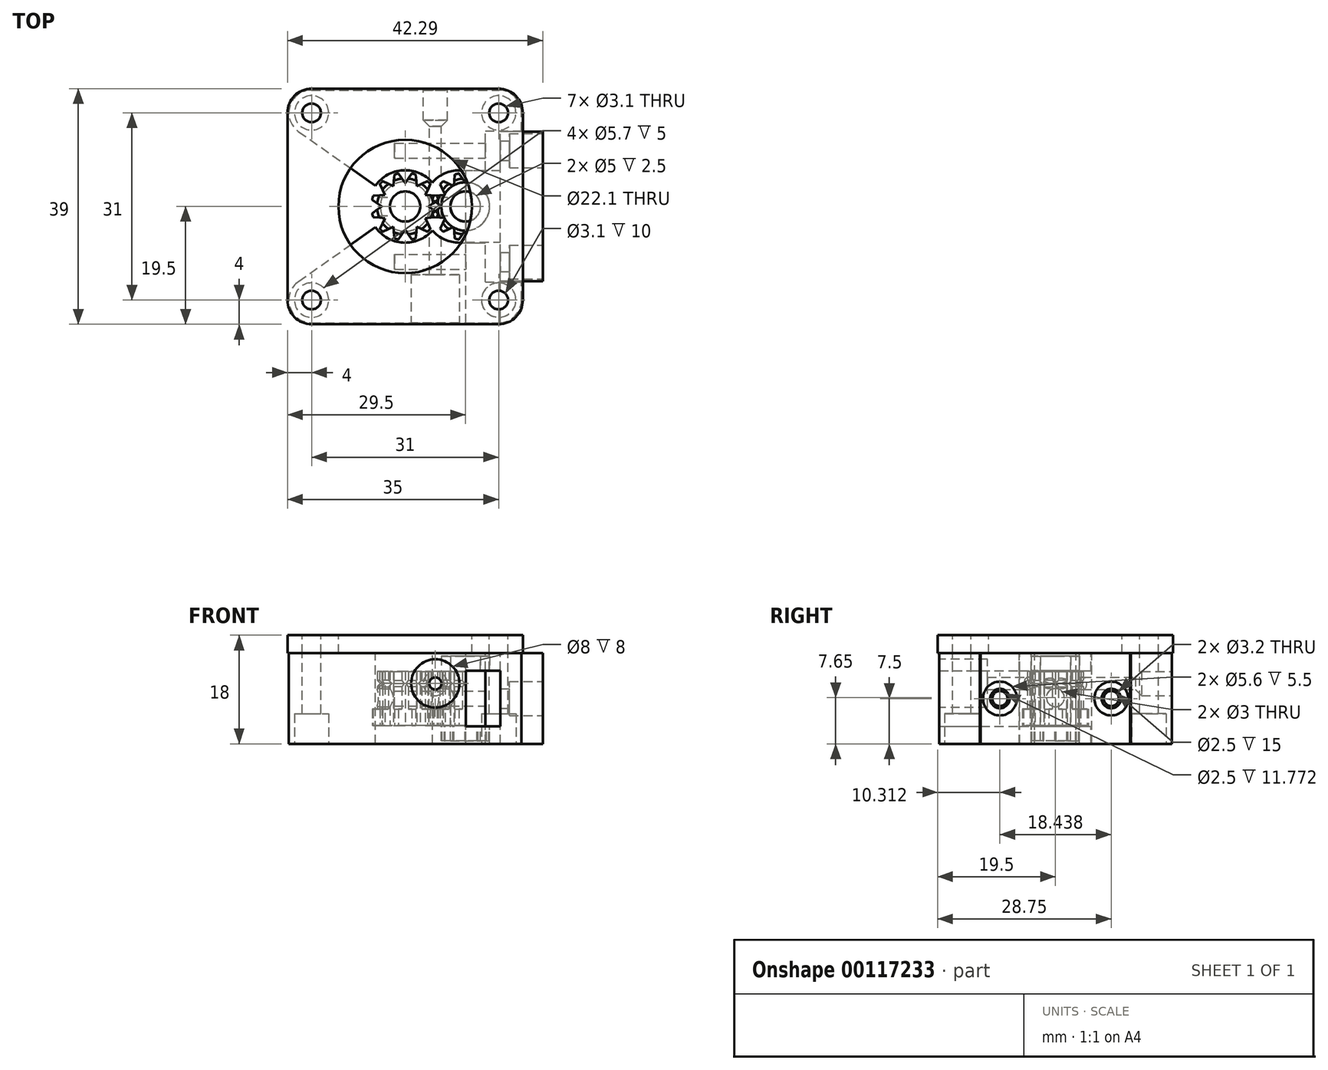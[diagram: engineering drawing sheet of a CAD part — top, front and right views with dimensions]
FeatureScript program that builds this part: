
annotation { "Feature Type Name" : "Feature", "Feature Type Description" : "" }
export const myFeature = defineFeature(function(context is Context, id is Id, definition is map)
    precondition{}
    {
        {
            var Q0;
            Q0=qCreatedBy(makeId("Top.planeOp"),FACE);
            var sketch = newSketch(context, id + "F0", { "sketchPlane" : qUnion([Q0])});
            skCircle(sketch, "E0", {"center": v(0, 0) * mm, "radius": 2.5 * mm});
            skCircle(sketch, "E1", {"center": v(0, 0) * mm, "radius": 5.58 * mm});
            skSolve(sketch);
        }
        {
            var Q0;
            Q0=makeQuery(id+"F0.imprint","IMPRINT",FACE,{"disambiguationData":[TD([[makeQuery(id+"F0.imprint","IMPRINT",EDGE,{"derivedFrom":sQuery(id+"F0.wireOp",EDGE,"E0")}),-1.0]])]});
            extrude(context, id + "F1", {"entities" : qUnion([Q0]), "depth" : 2.75 * mm});
        }
        {
            var Q0;
            Q0=makeQuery(id+"F1.opExtrude","CAP_FACE",FACE,{"disambiguationData":[OSD([sQuery(id+"F0.wireOp",EDGE,"E0"),sQuery(id+"F0.wireOp",EDGE,"E1")])],"isStart":false});
            var sketch = newSketch(context, id + "F2", { "sketchPlane" : qUnion([Q0])});
            skCircle(sketch, "E2", {"center": v(0, 0) * mm, "radius": 2.5 * mm});
            skCircle(sketch, "E3", {"center": v(0, 0) * mm, "radius": 4.65 * mm});
            skSolve(sketch);
        }
        {
            var Q0;
            Q0=makeQuery(id+"F2.imprint","IMPRINT",FACE,{"disambiguationData":[TD([[makeQuery(id+"F2.imprint","IMPRINT",EDGE,{"derivedFrom":sQuery(id+"F2.wireOp",EDGE,"E2")}),-1.0]])]});
            extrude(context, id + "F3", {"entities" : qUnion([Q0]), "operationType" : NewBodyOperationType.ADD, "depth" : (9 - 2.75) * mm});
        }
        {
            var Q0;
            Q0=qCreatedBy(makeId("Right.planeOp"),FACE);
            var sketch = newSketch(context, id + "F4", { "sketchPlane" : qUnion([Q0])});
            skLineSegment(sketch, "E4", {"start": v(0, -4.4) * mm, "end": v(0, 15.22) * mm, "construction": true});
            skLineSegment(sketch, "E5", {"start": v(4.1, 14.73) * mm, "end": v(4.1, -6.8) * mm, "construction": true});
            skLineSegment(sketch, "E6", {"start": v(6.69, 7) * mm, "end": v(-11.79, 7) * mm, "construction": true});
            skLineSegment(sketch, "E7", {"start": v(4.1, 7) * mm, "end": v(5.02, 7.92) * mm});
            skLineSegment(sketch, "E8", {"start": v(4.1, 7) * mm, "end": v(5.2, 5.9) * mm});
            skLineSegment(sketch, "E9", {"start": v(5.02, 7.92) * mm, "end": v(5.2, 5.9) * mm});
            skSolve(sketch);
        }
        {
            var Q0;
            Q0=makeQuery(id+"F4.imprint","IMPRINT",FACE,{"disambiguationData":[TD([[makeQuery(id+"F4.imprint","IMPRINT",EDGE,{"derivedFrom":sQuery(id+"F4.wireOp",EDGE,"E7")}),-1.0]])]});
            var Q1;
            Q1=sQuery(id+"F4.wireOp",EDGE,"E4");
            revolve(context, id + "F5", {"operationType" : NewBodyOperationType.REMOVE, "entities" : qUnion([Q0]), "axis" : qUnion([Q1]), "revolveType" : RevolveType.FULL, "oppositeDirection" : true});
        }
        {
            var Q0;
            Q0=qCreatedBy(makeId("Right.planeOp"),FACE);
            var sketch = newSketch(context, id + "F6", { "sketchPlane" : qUnion([Q0])});
            skCircle(sketch, "E10", {"center": v(0, 4.65) * mm, "radius": 1.5 * mm});
            skSolve(sketch);
        }
        {
            var Q0;
            Q0=makeQuery(id+"F6.imprint","IMPRINT",FACE,{"disambiguationData":[TD([[makeQuery(id+"F6.imprint","IMPRINT",EDGE,{"derivedFrom":sQuery(id+"F6.wireOp",EDGE,"E10")}),1.0]])]});
            extrude(context, id + "F7", {"entities" : qUnion([Q0]), "operationType" : NewBodyOperationType.REMOVE, "oppositeDirection" : true, "depth" : 25 * mm});
        }
        {
            var Q0;
            Q0=makeQuery(id+"F1.opExtrude","CAP_FACE",FACE,{"disambiguationData":[OSD([sQuery(id+"F0.wireOp",EDGE,"E0"),sQuery(id+"F0.wireOp",EDGE,"E1")])],"isStart":true});
            var sketch = newSketch(context, id + "F8", { "sketchPlane" : qUnion([Q0])});
            skCircle(sketch, "E11", {"center": v(0, 0) * mm, "radius": 3.88 * mm});
            skLineSegment(sketch, "E12", {"start": v(-1.69, 6.28) * mm, "end": v(0, 3.88) * mm});
            skLineSegment(sketch, "E13", {"start": v(0, 3.88) * mm, "end": v(1.69, 6.28) * mm});
            skArc(sketch, "E14", {"start": v(1.69, 6.28) * mm, "mid": v(0, 6.5) * mm, "end": v(-1.69, 6.28) * mm});
            skLineSegment(sketch, "E15.1.0", {"start": v(-1.94, 3.36) * mm, "end": v(-1.68, 6.28) * mm});
            skLineSegment(sketch, "E15.1.1", {"start": v(-4.6, 4.6) * mm, "end": v(-1.94, 3.36) * mm});
            skArc(sketch, "E15.1.2", {"start": v(-1.68, 6.28) * mm, "mid": v(-3.25, 5.63) * mm, "end": v(-4.6, 4.6) * mm});
            skLineSegment(sketch, "E15.2.0", {"start": v(-3.36, 1.94) * mm, "end": v(-4.6, 4.6) * mm});
            skLineSegment(sketch, "E15.2.1", {"start": v(-6.28, 1.68) * mm, "end": v(-3.36, 1.94) * mm});
            skArc(sketch, "E15.2.2", {"start": v(-4.6, 4.6) * mm, "mid": v(-5.63, 3.25) * mm, "end": v(-6.28, 1.68) * mm});
            skLineSegment(sketch, "E15.3.0", {"start": v(-3.88, 0) * mm, "end": v(-6.28, 1.69) * mm});
            skLineSegment(sketch, "E15.3.1", {"start": v(-6.28, -1.69) * mm, "end": v(-3.87, 0) * mm});
            skArc(sketch, "E15.3.2", {"start": v(-6.28, 1.69) * mm, "mid": v(-6.5, 0) * mm, "end": v(-6.28, -1.69) * mm});
            skLineSegment(sketch, "E15.4.0", {"start": v(-3.36, -1.94) * mm, "end": v(-6.28, -1.68) * mm});
            skLineSegment(sketch, "E15.4.1", {"start": v(-4.6, -4.6) * mm, "end": v(-3.36, -1.94) * mm});
            skArc(sketch, "E15.4.2", {"start": v(-6.28, -1.68) * mm, "mid": v(-5.63, -3.25) * mm, "end": v(-4.6, -4.6) * mm});
            skLineSegment(sketch, "E15.5.0", {"start": v(-1.94, -3.36) * mm, "end": v(-4.6, -4.6) * mm});
            skLineSegment(sketch, "E15.5.1", {"start": v(-1.68, -6.28) * mm, "end": v(-1.94, -3.36) * mm});
            skArc(sketch, "E15.5.2", {"start": v(-4.6, -4.6) * mm, "mid": v(-3.25, -5.63) * mm, "end": v(-1.68, -6.28) * mm});
            skLineSegment(sketch, "E15.6.0", {"start": v(0, -3.88) * mm, "end": v(-1.69, -6.28) * mm});
            skLineSegment(sketch, "E15.6.1", {"start": v(1.69, -6.28) * mm, "end": v(0, -3.87) * mm});
            skArc(sketch, "E15.6.2", {"start": v(-1.69, -6.28) * mm, "mid": v(0, -6.5) * mm, "end": v(1.69, -6.28) * mm});
            skLineSegment(sketch, "E15.7.0", {"start": v(1.94, -3.36) * mm, "end": v(1.68, -6.28) * mm});
            skLineSegment(sketch, "E15.7.1", {"start": v(4.6, -4.6) * mm, "end": v(1.94, -3.36) * mm});
            skArc(sketch, "E15.7.2", {"start": v(1.68, -6.28) * mm, "mid": v(3.25, -5.63) * mm, "end": v(4.6, -4.6) * mm});
            skLineSegment(sketch, "E15.8.0", {"start": v(3.36, -1.94) * mm, "end": v(4.6, -4.6) * mm});
            skLineSegment(sketch, "E15.8.1", {"start": v(6.28, -1.68) * mm, "end": v(3.36, -1.94) * mm});
            skArc(sketch, "E15.8.2", {"start": v(4.6, -4.6) * mm, "mid": v(5.63, -3.25) * mm, "end": v(6.28, -1.68) * mm});
            skLineSegment(sketch, "E15.9.0", {"start": v(3.88, 0) * mm, "end": v(6.28, -1.69) * mm});
            skLineSegment(sketch, "E15.9.1", {"start": v(6.28, 1.69) * mm, "end": v(3.87, 0) * mm});
            skArc(sketch, "E15.9.2", {"start": v(6.28, -1.69) * mm, "mid": v(6.5, 0) * mm, "end": v(6.28, 1.69) * mm});
            skLineSegment(sketch, "E15.10.0", {"start": v(3.36, 1.94) * mm, "end": v(6.28, 1.68) * mm});
            skLineSegment(sketch, "E15.10.1", {"start": v(4.6, 4.6) * mm, "end": v(3.36, 1.94) * mm});
            skArc(sketch, "E15.10.2", {"start": v(6.28, 1.68) * mm, "mid": v(5.63, 3.25) * mm, "end": v(4.6, 4.6) * mm});
            skLineSegment(sketch, "E15.11.0", {"start": v(1.94, 3.36) * mm, "end": v(4.6, 4.6) * mm});
            skLineSegment(sketch, "E15.11.1", {"start": v(1.68, 6.28) * mm, "end": v(1.94, 3.36) * mm});
            skArc(sketch, "E15.11.2", {"start": v(4.6, 4.6) * mm, "mid": v(3.25, 5.63) * mm, "end": v(1.68, 6.28) * mm});
            skSolve(sketch);
        }
        {
            var Q0;
            Q0 = qSketchRegion(id + "F8", true);
            extrude(context, id + "F9", {"entities" : qUnion([Q0]), "operationType" : NewBodyOperationType.REMOVE, "oppositeDirection" : true, "depth" : 25 * mm});
        }
        {
            var Q0;
            Q0=makeQuery(id+"F3.opExtrude","CAP_FACE",FACE,{"disambiguationData":[OSD([sQuery(id+"F2.wireOp",EDGE,"E2"),sQuery(id+"F2.wireOp",EDGE,"E3")])],"isStart":false});
            cPlane(context, id + "F10", {"entities" : qUnion([Q0]), "cplaneType" : CPlaneType.OFFSET, "offset" : 6 * mm, "width" : 150 * mm, "height" : 150 * mm});
        }
        {
            var Q0;
            Q0=qCreatedBy(id+"F10.planeOp",FACE);
            var sketch = newSketch(context, id + "F11", { "sketchPlane" : qUnion([Q0])});
            skCircle(sketch, "E16", {"center": v(0, 0) * mm, "radius": 11.05 * mm});
            skLineSegment(sketch, "E17.bottom", {"start": v(19.5, -19.5) * mm, "end": v(-19.5, -19.5) * mm});
            skLineSegment(sketch, "E17.top", {"start": v(19.5, 19.5) * mm, "end": v(-19.5, 19.5) * mm});
            skLineSegment(sketch, "E17.left", {"start": v(19.5, -19.5) * mm, "end": v(19.5, 19.5) * mm});
            skLineSegment(sketch, "E17.right", {"start": v(-19.5, -19.5) * mm, "end": v(-19.5, 19.5) * mm});
            skLineSegment(sketch, "E18.bottom", {"start": v(15.5, -15.5) * mm, "end": v(-15.5, -15.5) * mm, "construction": true});
            skLineSegment(sketch, "E18.top", {"start": v(15.5, 15.5) * mm, "end": v(-15.5, 15.5) * mm, "construction": true});
            skLineSegment(sketch, "E18.left", {"start": v(15.5, -15.5) * mm, "end": v(15.5, 15.5) * mm, "construction": true});
            skLineSegment(sketch, "E18.right", {"start": v(-15.5, -15.5) * mm, "end": v(-15.5, 15.5) * mm, "construction": true});
            skCircle(sketch, "E19", {"center": v(-15.5, 15.5) * mm, "radius": 1.55 * mm});
            skCircle(sketch, "E20.0.1.0", {"center": v(-15.5, -15.5) * mm, "radius": 1.55 * mm});
            skCircle(sketch, "E20.1.0.0", {"center": v(15.5, 15.5) * mm, "radius": 1.55 * mm});
            skCircle(sketch, "E20.1.1.0", {"center": v(15.5, -15.5) * mm, "radius": 1.55 * mm});
            skCircle(sketch, "E20.2.0.0", {"center": v(46.5, 15.5) * mm, "radius": 1.55 * mm});
            skCircle(sketch, "E20.2.1.0", {"center": v(46.5, -15.5) * mm, "radius": 1.55 * mm});
            skLineSegment(sketch, "E20.direction1", {"start": v(-15.5, 15.5) * mm, "end": v(15.5, 15.5) * mm, "construction": true});
            skLineSegment(sketch, "E20.direction2", {"start": v(-15.5, 15.5) * mm, "end": v(-15.5, -15.5) * mm, "construction": true});
            skSolve(sketch);
        }
        {
            var Q0;
            Q0=makeQuery(id+"F11.imprint","IMPRINT",FACE,{"disambiguationData":[TD([[makeQuery(id+"F11.imprint","IMPRINT",EDGE,{"derivedFrom":sQuery(id+"F11.wireOp",EDGE,"E16")}),-1.0]])]});
            extrude(context, id + "F12", {"entities" : qUnion([Q0]), "oppositeDirection" : true, "depth" : 3 * mm});
        }
        {
            var Q0;
            Q0=makeQuery(id+"F1.opExtrude","SWEPT_BODY",BODY,{"disambiguationData":[OSD([sQuery(id+"F0.wireOp",EDGE,"E0"),sQuery(id+"F0.wireOp",EDGE,"E1")])]});
            transform(context, id + "F13", {"entities" : qUnion([Q0]), "transformType" : TransformType.TRANSLATION_3D, "dx" : 10 * mm, "dy" : 0 * mm, "dz" : 0 * mm, "makeCopy" : true});
        }
        {
            var Q0;
            Q0=makeQuery(id+"F13.opPattern","COPY",FACE,{"derivedFrom":makeQuery(id+"F1.opExtrude","CAP_FACE",FACE,{"disambiguationData":[OSD([sQuery(id+"F0.wireOp",EDGE,"E0"),sQuery(id+"F0.wireOp",EDGE,"E1")])],"isStart":true}),"instanceName":"1"});
            var sketch = newSketch(context, id + "F14", { "sketchPlane" : qUnion([Q0])});
            skCircle(sketch, "E21", {"center": v(10, 0) * mm, "radius": 2.5 * mm});
            skCircle(sketch, "E22", {"center": v(10, 0) * mm, "radius": 4 * mm});
            skSolve(sketch);
        }
        {
            var Q0;
            Q0=makeQuery(id+"F14.imprint","IMPRINT",FACE,{"disambiguationData":[TD([[makeQuery(id+"F14.imprint","IMPRINT",EDGE,{"derivedFrom":sQuery(id+"F14.wireOp",EDGE,"E21")}),1.0]])]});
            extrude(context, id + "F15", {"entities" : qUnion([Q0]), "depth" : 2.5 * mm});
        }
        {
            var Q0;
            Q0=makeQuery(id+"F13.opPattern","COPY",FACE,{"derivedFrom":makeQuery(id+"F3.opExtrude","CAP_FACE",FACE,{"disambiguationData":[OSD([sQuery(id+"F2.wireOp",EDGE,"E2"),sQuery(id+"F2.wireOp",EDGE,"E3")])],"isStart":false}),"instanceName":"1"});
            var sketch = newSketch(context, id + "F16", { "sketchPlane" : qUnion([Q0])});
            skCircle(sketch, "E23", {"center": v(10, 0) * mm, "radius": 2.5 * mm});
            skCircle(sketch, "E24", {"center": v(10, 0) * mm, "radius": 4 * mm});
            skSolve(sketch);
        }
        {
            var Q0;
            Q0 = qSketchRegion(id + "F16", true);
            extrude(context, id + "F17", {"entities" : qUnion([Q0]), "depth" : 2.5 * mm});
        }
        {
            var Q0;
            Q0=makeQuery(id+"F17.opExtrude","CAP_FACE",FACE,{"disambiguationData":[OSD([sQuery(id+"F16.wireOp",EDGE,"E23"),sQuery(id+"F16.wireOp",EDGE,"E24")])],"isStart":false});
            var sketch = newSketch(context, id + "F18", { "sketchPlane" : qUnion([Q0])});
            skCircle(sketch, "E25", {"center": v(10, 0) * mm, "radius": 2.5 * mm});
            skSolve(sketch);
        }
        {
            var Q0;
            Q0 = qSketchRegion(id + "F18", true);
            var Q1;
            Q1=makeQuery(id+"F15.opExtrude","CAP_FACE",FACE,{"disambiguationData":[OSD([sQuery(id+"F8.wireOp",EDGE,"E12"),sQuery(id+"F8.wireOp",EDGE,"E13"),sQuery(id+"F8.wireOp",EDGE,"E15.1.0"),sQuery(id+"F8.wireOp",EDGE,"E15.1.1"),sQuery(id+"F8.wireOp",EDGE,"E15.2.0"),sQuery(id+"F8.wireOp",EDGE,"E15.2.1"),sQuery(id+"F8.wireOp",EDGE,"E15.3.0"),sQuery(id+"F8.wireOp",EDGE,"E15.3.1"),sQuery(id+"F8.wireOp",EDGE,"E15.4.0"),sQuery(id+"F8.wireOp",EDGE,"E15.4.1"),sQuery(id+"F8.wireOp",EDGE,"E15.5.0"),sQuery(id+"F8.wireOp",EDGE,"E15.5.1"),sQuery(id+"F8.wireOp",EDGE,"E15.6.0"),sQuery(id+"F8.wireOp",EDGE,"E15.6.1"),sQuery(id+"F8.wireOp",EDGE,"E15.7.0"),sQuery(id+"F8.wireOp",EDGE,"E15.7.1"),sQuery(id+"F8.wireOp",EDGE,"E15.8.0"),sQuery(id+"F8.wireOp",EDGE,"E15.8.1"),sQuery(id+"F8.wireOp",EDGE,"E15.9.0"),sQuery(id+"F8.wireOp",EDGE,"E15.9.1"),sQuery(id+"F8.wireOp",EDGE,"E15.10.0"),sQuery(id+"F8.wireOp",EDGE,"E15.10.1"),sQuery(id+"F8.wireOp",EDGE,"E15.11.0"),sQuery(id+"F8.wireOp",EDGE,"E15.11.1"),sQuery(id+"F14.wireOp",EDGE,"E21"),sQuery(id+"F14.wireOp",EDGE,"E22")])],"isStart":false});
            extrude(context, id + "F19", {"entities" : qUnion([Q0]), "endBound" : BoundingType.UP_TO_SURFACE, "oppositeDirection" : true, "endBoundEntityFace" : qUnion([Q1]), "depth" : 25 * mm});
        }
        {
            var Q0;
            Q0=makeQuery(id+"F12.opExtrude","CAP_FACE",FACE,{"disambiguationData":[OSD([sQuery(id+"F11.wireOp",EDGE,"E16"),sQuery(id+"F11.wireOp",EDGE,"E17.bottom"),sQuery(id+"F11.wireOp",EDGE,"E17.top"),sQuery(id+"F11.wireOp",EDGE,"E17.left"),sQuery(id+"F11.wireOp",EDGE,"E17.right"),sQuery(id+"F11.wireOp",EDGE,"E19"),sQuery(id+"F11.wireOp",EDGE,"E20.0.1.0"),sQuery(id+"F11.wireOp",EDGE,"E20.1.0.0"),sQuery(id+"F11.wireOp",EDGE,"E20.1.1.0")])],"isStart":false});
            var sketch = newSketch(context, id + "F20", { "sketchPlane" : qUnion([Q0])});
            skArc(sketch, "E26", {"start": v(4.5, 3.97) * mm, "mid": v(-0.33, 6) * mm, "end": v(-4.9, 3.45) * mm});
            skArc(sketch, "E27", {"start": v(9, 6) * mm, "mid": v(6.53, 5.47) * mm, "end": v(4.5, 3.97) * mm});
            skLineSegment(sketch, "E28.bottom", {"start": v(9, 6) * mm, "end": v(13.27, 6) * mm});
            skLineSegment(sketch, "E28.top", {"start": v(9, -6) * mm, "end": v(13.27, -6) * mm});
            skArc(sketch, "E29.trimOffspring", {"start": v(4.5, -3.97) * mm, "mid": v(6.53, -5.47) * mm, "end": v(9, -6) * mm});
            skLineSegment(sketch, "E30.bottom", {"start": v(-15.5, 19.27) * mm, "end": v(15.5, 19.27) * mm});
            skLineSegment(sketch, "E30.top", {"start": v(-15.5, -19.27) * mm, "end": v(15.5, -19.27) * mm});
            skLineSegment(sketch, "E30.right", {"start": v(19.27, 15.5) * mm, "end": v(19.27, 12.5) * mm});
            skCircle(sketch, "E31", {"center": v(15.5, 15.5) * mm, "radius": 1.55 * mm});
            skCircle(sketch, "E32", {"center": v(15.5, -15.5) * mm, "radius": 1.55 * mm});
            skCircle(sketch, "E33", {"center": v(-15.5, -15.5) * mm, "radius": 1.55 * mm});
            skArc(sketch, "E34", {"start": v(19.27, 15.5) * mm, "mid": v(18.16, 18.16) * mm, "end": v(15.5, 19.27) * mm});
            skArc(sketch, "E35", {"start": v(15.5, -19.27) * mm, "mid": v(18.16, -18.16) * mm, "end": v(19.27, -15.5) * mm});
            skArc(sketch, "E36", {"start": v(-17.67, -12.42) * mm, "mid": v(-19.1, -16.64) * mm, "end": v(-15.5, -19.27) * mm});
            skLineSegment(sketch, "E37", {"start": v(-17.67, -12.42) * mm, "end": v(-4.9, -3.45) * mm});
            skArc(sketch, "E38", {"start": v(-15.5, 19.27) * mm, "mid": v(-19.1, 16.64) * mm, "end": v(-17.67, 12.42) * mm});
            skLineSegment(sketch, "E39", {"start": v(-17.67, 12.42) * mm, "end": v(-4.9, 3.45) * mm});
            skArc(sketch, "E40.trimOffspring", {"start": v(-4.9, -3.45) * mm, "mid": v(-0.33, -6) * mm, "end": v(4.5, -3.97) * mm});
            skLineSegment(sketch, "E41.bottom", {"start": v(13.27, 12.5) * mm, "end": v(19.27, 12.5) * mm});
            skLineSegment(sketch, "E41.top", {"start": v(13.27, -12.5) * mm, "end": v(19.27, -12.5) * mm});
            skLineSegment(sketch, "E41.left", {"start": v(13.27, 12.5) * mm, "end": v(13.27, 6) * mm});
            skPoint(sketch, "E41.middle", {"position": v(19.27, 0) * mm});
            skPoint(sketch, "E41.cornerSnap0", {"position": v(13.27, 6) * mm});
            skLineSegment(sketch, "E42.trimOffspring", {"start": v(13.27, -6) * mm, "end": v(13.27, -12.5) * mm});
            skPoint(sketch, "E28.right.start.orphan", {"position": v(17.53, 6) * mm});
            skPoint(sketch, "E41.right.end.orphan", {"position": v(25.27, -12.5) * mm});
            skPoint(sketch, "E41.right.start.orphan", {"position": v(25.27, 12.5) * mm});
            skLineSegment(sketch, "E43.trimOffspring", {"start": v(19.27, -12.5) * mm, "end": v(19.27, -15.5) * mm});
            skSolve(sketch);
        }
        {
            var Q0;
            Q0=makeQuery(id+"F20.imprint","IMPRINT",FACE,{"disambiguationData":[TD([[makeQuery(id+"F20.imprint","IMPRINT",EDGE,{"derivedFrom":sQuery(id+"F20.wireOp",EDGE,"E30.bottom")}),-1.0]])]});
            var Q1;
            {var subQ4=sQuery(id+"F20.wireOp",EDGE,"E29.trimOffspring");Q1=makeQuery(id+"F20.imprint","IMPRINT",FACE,{"disambiguationData":[TD([[makeQuery(id+"F20.imprint","IMPRINT",EDGE,{"derivedFrom":subQ4}),-1.0]])]});}
            var Q2;
            Q2=makeQuery(id+"F20.imprint","IMPRINT",FACE,{"disambiguationData":[TD([[makeQuery(id+"F20.imprint","IMPRINT",EDGE,{"derivedFrom":sQuery(id+"F20.wireOp",EDGE,"E30.top")}),1.0]])]});
            var Q3;
            {var subQ5=sQuery(id+"F20.wireOp",EDGE,"E26");Q3=makeQuery(id+"F20.imprint","IMPRINT",FACE,{"disambiguationData":[TD([[makeQuery(id+"F20.imprint","IMPRINT",EDGE,{"derivedFrom":subQ5}),-1.0]])]});}
            extrude(context, id + "F21", {"entities" : qUnion([Q0, Q1, Q2, Q3]), "depth" : 15 * mm});
        }
        {
            var Q0;
            Q0=makeQuery(id+"F20.imprint","IMPRINT",FACE,{"disambiguationData":[TD([[makeQuery(id+"F20.imprint","IMPRINT",EDGE,{"derivedFrom":sQuery(id+"F20.wireOp",EDGE,"E30.top")}),1.0]])]});
            extrude(context, id + "F22", {"entities" : qUnion([Q0]), "depth" : 15 * mm});
        }
        {
            var Q0;
            Q0=makeQuery(id+"F22.opExtrude","SWEPT_FACE",FACE,{"disambiguationData":[OSD([sQuery(id+"F20.wireOp",EDGE,"E42.trimOffspring")])]});
            var sketch = newSketch(context, id + "F23", { "sketchPlane" : qUnion([Q0])});
            skLineSegment(sketch, "E44", {"start": v(12.5, 12) * mm, "end": v(6, -3) * mm, "construction": true});
            skLineSegment(sketch, "E45", {"start": v(-12.35, 12) * mm, "end": v(-6.02, -3) * mm, "construction": true});
            skCircle(sketch, "E46", {"center": v(9.25, 4.5) * mm, "radius": 1.25 * mm});
            skCircle(sketch, "E47", {"center": v(-9.19, 4.5) * mm, "radius": 1.25 * mm});
            skSolve(sketch);
        }
        {
            var Q0;
            Q0 = qSketchRegion(id + "F23", true);
            extrude(context, id + "F24", {"entities" : qUnion([Q0]), "operationType" : NewBodyOperationType.REMOVE, "oppositeDirection" : true, "depth" : 15 * mm});
        }
        {
            var Q0;
            Q0=makeQuery(id+"F20.imprint","IMPRINT",FACE,{"disambiguationData":[TD([[makeQuery(id+"F20.imprint","IMPRINT",EDGE,{"derivedFrom":sQuery(id+"F20.wireOp",EDGE,"E30.bottom")}),1.0]])]});
            var sketch = newSketch(context, id + "F25", { "sketchPlane" : qUnion([Q0])});
            skLineSegment(sketch, "E48.bottom", {"start": v(10.04, 5.9) * mm, "end": v(15.79, 5.9) * mm});
            skLineSegment(sketch, "E48.top", {"start": v(10.04, -5.9) * mm, "end": v(15.79, -5.9) * mm});
            skLineSegment(sketch, "E48.left", {"start": v(10.04, 5.9) * mm, "end": v(10.04, 4) * mm});
            skPoint(sketch, "E48.middle", {"position": v(19.29, 0) * mm});
            skLineSegment(sketch, "E49.trimOffspring", {"start": v(10.04, -4) * mm, "end": v(10.04, -5.9) * mm});
            skLineSegment(sketch, "E50.bottom", {"start": v(22.79, 12.38) * mm, "end": v(15.79, 12.38) * mm});
            skLineSegment(sketch, "E50.top", {"start": v(22.79, -12.38) * mm, "end": v(15.79, -12.38) * mm});
            skLineSegment(sketch, "E50.left", {"start": v(22.79, 12.38) * mm, "end": v(22.79, -12.38) * mm});
            skLineSegment(sketch, "E50.right", {"start": v(15.79, 12.38) * mm, "end": v(15.79, 5.9) * mm});
            skLineSegment(sketch, "E51.trimOffspring", {"start": v(15.79, -5.9) * mm, "end": v(15.79, -12.38) * mm});
            skPoint(sketch, "E48.right.start.orphan", {"position": v(28.54, 5.9) * mm});
            skPoint(sketch, "E52.trimOffspring.end.orphan", {"position": v(28.54, -5.9) * mm});
            skArc(sketch, "E53", {"start": v(10.04, -4) * mm, "mid": v(14, 0) * mm, "end": v(10.04, 4) * mm});
            skSolve(sketch);
        }
        {
            var Q0;
            Q0 = qSketchRegion(id + "F25", true);
            extrude(context, id + "F26", {"entities" : qUnion([Q0]), "depth" : 15 * mm});
        }
        {
            var Q0;
            Q0=makeQuery(id+"F26.opExtrude","SWEPT_FACE",FACE,{"disambiguationData":[OSD([sQuery(id+"F25.wireOp",EDGE,"E50.left")])]});
            var sketch = newSketch(context, id + "F27", { "sketchPlane" : qUnion([Q0])});
            skCircle(sketch, "E54", {"center": v(-9.19, 4.5) * mm, "radius": 1.6 * mm});
            skCircle(sketch, "E55", {"center": v(9.25, 4.5) * mm, "radius": 1.6 * mm});
            skSolve(sketch);
        }
        {
            var Q0;
            Q0 = qSketchRegion(id + "F27", true);
            extrude(context, id + "F28", {"entities" : qUnion([Q0]), "operationType" : NewBodyOperationType.REMOVE, "oppositeDirection" : true, "depth" : 8 * mm});
        }
        {
            var Q0;
            Q0=makeQuery(id+"F26.opExtrude","SWEPT_FACE",FACE,{"disambiguationData":[OSD([sQuery(id+"F25.wireOp",EDGE,"E50.left")])]});
            var sketch = newSketch(context, id + "F29", { "sketchPlane" : qUnion([Q0])});
            skCircle(sketch, "E56", {"center": v(-9.19, 4.5) * mm, "radius": 2.8 * mm});
            skCircle(sketch, "E57", {"center": v(9.25, 4.5) * mm, "radius": 2.8 * mm});
            skSolve(sketch);
        }
        {
            var Q0;
            Q0 = qSketchRegion(id + "F29", true);
            extrude(context, id + "F30", {"entities" : qUnion([Q0]), "operationType" : NewBodyOperationType.REMOVE, "oppositeDirection" : true, "depth" : 5.5 * mm});
        }
        {
            var Q0;
            Q0=makeQuery(id+"F22.opExtrude","SWEPT_BODY",BODY,{"disambiguationData":[OSD([sQuery(id+"F11.wireOp",EDGE,"E16"),sQuery(id+"F20.wireOp",EDGE,"E28.top"),sQuery(id+"F20.wireOp",EDGE,"E30.top"),sQuery(id+"F20.wireOp",EDGE,"E32"),sQuery(id+"F20.wireOp",EDGE,"E33"),sQuery(id+"F20.wireOp",EDGE,"E35"),sQuery(id+"F20.wireOp",EDGE,"E36"),sQuery(id+"F20.wireOp",EDGE,"E37"),sQuery(id+"F20.wireOp",EDGE,"E41.top"),sQuery(id+"F20.wireOp",EDGE,"E42.trimOffspring"),sQuery(id+"F20.wireOp",EDGE,"E43.trimOffspring")])]});
            deleteBodies(context, id + "F31", {"entities" : qUnion([Q0])});
        }
        {
            var Q0;
            Q0=makeQuery(id+"F21.opExtrude","SWEPT_FACE",FACE,{"disambiguationData":[OSD([sQuery(id+"F20.wireOp",EDGE,"E30.top")])]});
            var sketch = newSketch(context, id + "F32", { "sketchPlane" : qUnion([Q0])});
            skLineSegment(sketch, "E58", {"start": v(-7.91, 7) * mm, "end": v(6.12, 7) * mm, "construction": true});
            skLineSegment(sketch, "E59", {"start": v(-5, 17.58) * mm, "end": v(-5, -8.26) * mm, "construction": true});
            skCircle(sketch, "E60", {"center": v(-5, 7) * mm, "radius": 1 * mm});
            skSolve(sketch);
        }
        {
            var Q0;
            Q0 = qSketchRegion(id + "F32", true);
            extrude(context, id + "F33", {"entities" : qUnion([Q0]), "operationType" : NewBodyOperationType.REMOVE, "endBound" : BoundingType.THROUGH_ALL, "oppositeDirection" : true, "depth" : 25 * mm});
        }
        {
            var Q0;
            Q0=makeQuery(id+"F21.opExtrude","SWEPT_FACE",FACE,{"disambiguationData":[OSD([sQuery(id+"F20.wireOp",EDGE,"E30.bottom")])]});
            var sketch = newSketch(context, id + "F34", { "sketchPlane" : qUnion([Q0])});
            skLineSegment(sketch, "E61", {"start": v(-15.5, 7) * mm, "end": v(15.5, 7) * mm, "construction": true});
            skLineSegment(sketch, "E62", {"start": v(5, 21.97) * mm, "end": v(5, -13.87) * mm, "construction": true});
            skLineSegment(sketch, "E63", {"start": v(0, 22.79) * mm, "end": v(0, -28.24) * mm, "construction": true});
            skPoint(sketch, "E63.endSnap0", {"position": v(0, -3) * mm});
            skCircle(sketch, "E64", {"center": v(5, 7) * mm, "radius": 1 * mm});
            skSolve(sketch);
        }
        {
            var Q0;
            Q0 = qSketchRegion(id + "F34", true);
            extrude(context, id + "F35", {"entities" : qUnion([Q0]), "operationType" : NewBodyOperationType.REMOVE, "endBound" : BoundingType.THROUGH_ALL, "oppositeDirection" : true, "depth" : 25 * mm});
        }
        {
            var Q0;
            Q0=makeQuery(id+"F21.opExtrude","SWEPT_FACE",FACE,{"disambiguationData":[OSD([sQuery(id+"F20.wireOp",EDGE,"E30.bottom")])]});
            var sketch = newSketch(context, id + "F36", { "sketchPlane" : qUnion([Q0])});
            skCircle(sketch, "E65", {"center": v(5, 7) * mm, "radius": 4 * mm});
            skSolve(sketch);
        }
        {
            var Q0;
            Q0 = qSketchRegion(id + "F36", true);
            extrude(context, id + "F37", {"entities" : qUnion([Q0]), "operationType" : NewBodyOperationType.REMOVE, "oppositeDirection" : true, "depth" : 8 * mm});
        }
        {
            var Q0;
            Q0=makeQuery(id+"F21.opExtrude","SWEPT_FACE",FACE,{"disambiguationData":[OSD([sQuery(id+"F20.wireOp",EDGE,"E30.top")])]});
            var sketch = newSketch(context, id + "F38", { "sketchPlane" : qUnion([Q0])});
            skCircle(sketch, "E66", {"center": v(-5, 7) * mm, "radius": 2 * mm});
            skSolve(sketch);
        }
        {
            var Q0;
            Q0 = qSketchRegion(id + "F38", true);
            extrude(context, id + "F39", {"entities" : qUnion([Q0]), "operationType" : NewBodyOperationType.REMOVE, "oppositeDirection" : true, "depth" : 4 * mm});
        }
        {
            var Q0;
            Q0=makeQuery(id+"F39.boolean.opBoolean","INTERSECT",EDGE,{"derivedFrom":[makeQuery(id+"F33.boolean.opBoolean","COPY",FACE,{"derivedFrom":makeQuery(id+"F33.opExtrude","SWEPT_FACE",FACE,{"disambiguationData":[OSD([sQuery(id+"F32.wireOp",EDGE,"E60")])]})}),makeQuery(id+"F39.opExtrude","CAP_FACE",FACE,{"disambiguationData":[OSD([sQuery(id+"F38.wireOp",EDGE,"E66")])],"isStart":false})]});
            chamfer(context, id + "F40", {"entities" : qUnion([Q0]), "width" : 2 * mm, "tangentPropagation" : true});
        }
        {
            var Q0;
            Q0=makeQuery(id+"F21.opExtrude","CAP_FACE",FACE,{"disambiguationData":[OSD([sQuery(id+"F11.wireOp",EDGE,"E20.0.1.0"),sQuery(id+"F20.wireOp",EDGE,"E26"),sQuery(id+"F20.wireOp",EDGE,"E27"),sQuery(id+"F20.wireOp",EDGE,"E28.bottom"),sQuery(id+"F20.wireOp",EDGE,"E30.bottom"),sQuery(id+"F20.wireOp",EDGE,"E30.right"),sQuery(id+"F20.wireOp",EDGE,"E31"),sQuery(id+"F20.wireOp",EDGE,"E34"),sQuery(id+"F20.wireOp",EDGE,"E38"),sQuery(id+"F20.wireOp",EDGE,"E39"),sQuery(id+"F20.wireOp",EDGE,"E41.bottom"),sQuery(id+"F20.wireOp",EDGE,"E41.left")])],"isStart":false});
            var sketch = newSketch(context, id + "F41", { "sketchPlane" : qUnion([Q0])});
            skCircle(sketch, "E67", {"center": v(-15.5, 15.5) * mm, "radius": 2.85 * mm});
            skCircle(sketch, "E68", {"center": v(15.5, 15.5) * mm, "radius": 2.85 * mm});
            skSolve(sketch);
        }
        {
            var Q0;
            Q0 = qSketchRegion(id + "F41", true);
            extrude(context, id + "F42", {"entities" : qUnion([Q0]), "operationType" : NewBodyOperationType.REMOVE, "oppositeDirection" : true, "depth" : 5 * mm});
        }
        {
            var Q0;
            Q0=makeQuery(id+"F21.opExtrude","CAP_FACE",FACE,{"disambiguationData":[OSD([sQuery(id+"F20.wireOp",EDGE,"E28.top"),sQuery(id+"F20.wireOp",EDGE,"E29.trimOffspring"),sQuery(id+"F20.wireOp",EDGE,"E30.top"),sQuery(id+"F20.wireOp",EDGE,"E32"),sQuery(id+"F20.wireOp",EDGE,"E33"),sQuery(id+"F20.wireOp",EDGE,"E35"),sQuery(id+"F20.wireOp",EDGE,"E36"),sQuery(id+"F20.wireOp",EDGE,"E37"),sQuery(id+"F20.wireOp",EDGE,"E40.trimOffspring"),sQuery(id+"F20.wireOp",EDGE,"E41.top"),sQuery(id+"F20.wireOp",EDGE,"E42.trimOffspring"),sQuery(id+"F20.wireOp",EDGE,"E43.trimOffspring")])],"isStart":false});
            var sketch = newSketch(context, id + "F43", { "sketchPlane" : qUnion([Q0])});
            skCircle(sketch, "E69", {"center": v(15.5, -15.5) * mm, "radius": 2.85 * mm});
            skCircle(sketch, "E70", {"center": v(-15.5, -15.5) * mm, "radius": 2.85 * mm});
            skSolve(sketch);
        }
        {
            var Q0;
            Q0 = qSketchRegion(id + "F43", true);
            extrude(context, id + "F44", {"entities" : qUnion([Q0]), "operationType" : NewBodyOperationType.REMOVE, "oppositeDirection" : true, "depth" : 5 * mm});
        }
        {
            var Q0;
            Q0=makeQuery(id+"F12.opExtrude","SWEPT_EDGE",EDGE,{"disambiguationData":[OSD([sQuery(id+"F11.wireOp",EDGE,"E17.bottom"),sQuery(id+"F11.wireOp",EDGE,"E17.left")])]});
            var Q1;
            Q1=makeQuery(id+"F12.opExtrude","SWEPT_EDGE",EDGE,{"disambiguationData":[OSD([sQuery(id+"F11.wireOp",EDGE,"E17.top"),sQuery(id+"F11.wireOp",EDGE,"E17.left")])]});
            var Q2;
            Q2=makeQuery(id+"F12.opExtrude","SWEPT_EDGE",EDGE,{"disambiguationData":[OSD([sQuery(id+"F11.wireOp",EDGE,"E17.top"),sQuery(id+"F11.wireOp",EDGE,"E17.right")])]});
            var Q3;
            Q3=makeQuery(id+"F12.opExtrude","SWEPT_EDGE",EDGE,{"disambiguationData":[OSD([sQuery(id+"F11.wireOp",EDGE,"E17.bottom"),sQuery(id+"F11.wireOp",EDGE,"E17.right")])]});
            fillet(context, id + "F45", {"entities" : qUnion([Q0, Q1, Q2, Q3]), "radius" : 4 * mm, "tangentPropagation" : true, "allowEdgeOverflow" : false});
        }
        {
            var Q0;
            Q0=makeQuery(id+"F26.opExtrude","SWEPT_FACE",FACE,{"disambiguationData":[OSD([sQuery(id+"F25.wireOp",EDGE,"E48.top")])]});
            var sketch = newSketch(context, id + "F46", { "sketchPlane" : qUnion([Q0])});
            skLineSegment(sketch, "E71.bottom", {"start": v(-15.79, 9.13) * mm, "end": v(-4.29, 9.13) * mm});
            skLineSegment(sketch, "E71.top", {"start": v(-15.79, -0.12) * mm, "end": v(-4.29, -0.12) * mm});
            skLineSegment(sketch, "E71.left", {"start": v(-15.79, 9.13) * mm, "end": v(-15.79, -0.12) * mm});
            skLineSegment(sketch, "E71.right", {"start": v(-4.29, 9.13) * mm, "end": v(-4.29, -0.12) * mm});
            skPoint(sketch, "E71.middle", {"position": v(-10.04, 4.5) * mm});
            skSolve(sketch);
        }
        {
            var Q0;
            {var subQ0=sQuery(id+"F46.wireOp",EDGE,"E71.left");Q0=makeQuery(id+"F46.imprint","IMPRINT",FACE,{"disambiguationData":[TD([[makeQuery(id+"F46.imprint","IMPRINT",EDGE,{"derivedFrom":subQ0}),-1.0]])]});}
            extrude(context, id + "F47", {"entities" : qUnion([Q0]), "operationType" : NewBodyOperationType.REMOVE, "endBound" : BoundingType.THROUGH_ALL, "oppositeDirection" : true, "depth" : 25 * mm});
        }
    });
